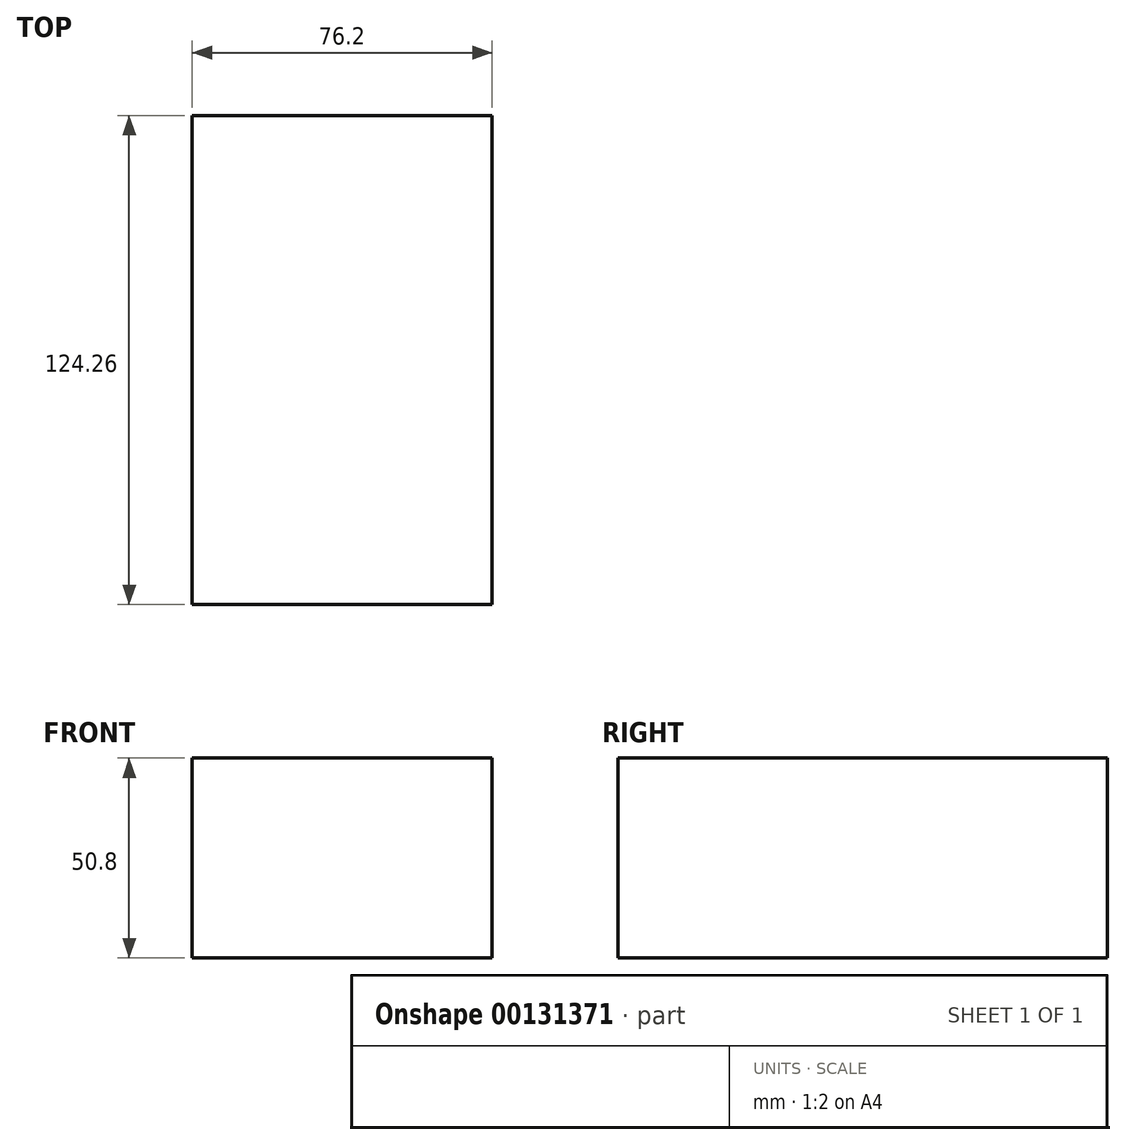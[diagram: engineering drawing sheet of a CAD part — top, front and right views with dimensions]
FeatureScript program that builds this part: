
annotation { "Feature Type Name" : "Feature", "Feature Type Description" : "" }
export const myFeature = defineFeature(function(context is Context, id is Id, definition is map)
    precondition{}
    {
        {
            var Q0;
            Q0=qCreatedBy(makeId("Front.planeOp"),FACE);
            var sketch = newSketch(context, id + "F0", { "sketchPlane" : qUnion([Q0])});
            skLineSegment(sketch, "E0.bottom", {"start": v(-62.79, 48) * mm, "end": v(13.41, 48) * mm});
            skLineSegment(sketch, "E0.top", {"start": v(-62.79, -2.8) * mm, "end": v(13.41, -2.8) * mm});
            skLineSegment(sketch, "E0.left", {"start": v(-62.79, 48) * mm, "end": v(-62.79, -2.8) * mm});
            skLineSegment(sketch, "E0.right", {"start": v(13.41, 48) * mm, "end": v(13.41, -2.8) * mm});
            skSolve(sketch);
        }
        {
            var Q0;
            Q0 = qSketchRegion(id + "F0", true);
            extrude(context, id + "F1", {"entities" : qUnion([Q0]), "endBound" : BoundingType.SYMMETRIC, "depth" : 124.26 * mm});
        }
    });
